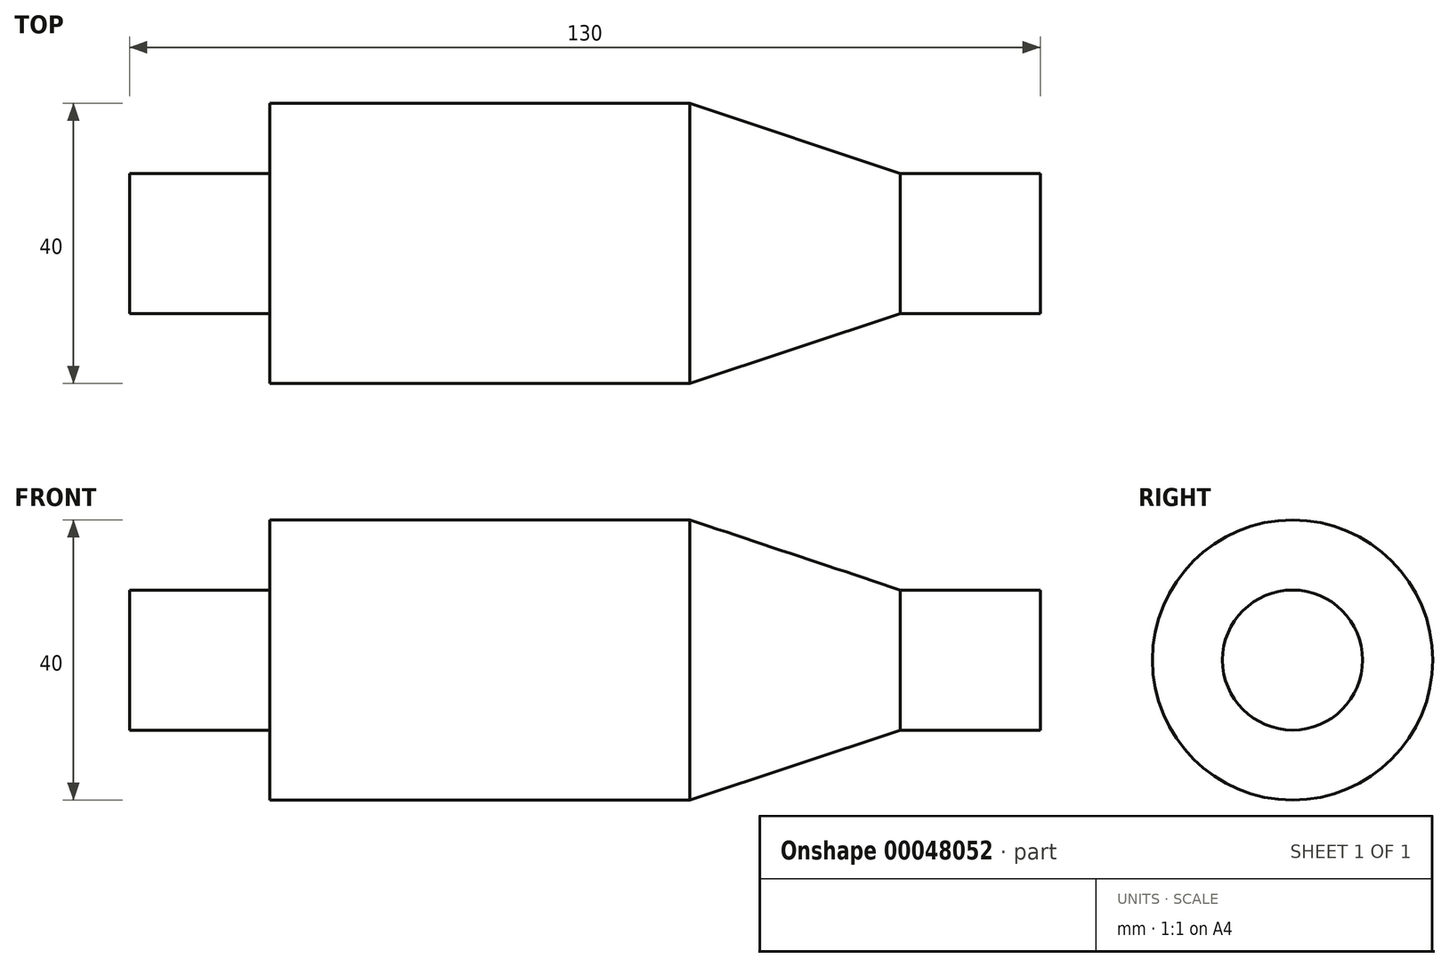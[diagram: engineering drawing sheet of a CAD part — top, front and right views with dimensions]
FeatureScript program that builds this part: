
annotation { "Feature Type Name" : "Feature", "Feature Type Description" : "" }
export const myFeature = defineFeature(function(context is Context, id is Id, definition is map)
    precondition{}
    {
        {
            var Q0;
            Q0=qCreatedBy(makeId("Front.planeOp"),FACE);
            var sketch = newSketch(context, id + "F0", { "sketchPlane" : qUnion([Q0])});
            skLineSegment(sketch, "E0", {"start": v(0, 0) * mm, "end": v(130, 0) * mm});
            skLineSegment(sketch, "E1", {"start": v(130, 0) * mm, "end": v(130, 10) * mm});
            skLineSegment(sketch, "E2", {"start": v(130, 10) * mm, "end": v(110, 10) * mm});
            skLineSegment(sketch, "E3", {"start": v(110, 10) * mm, "end": v(80, 20) * mm});
            skLineSegment(sketch, "E4", {"start": v(80, 20) * mm, "end": v(20, 20) * mm});
            skLineSegment(sketch, "E5", {"start": v(20, 20) * mm, "end": v(20, 10) * mm});
            skLineSegment(sketch, "E6", {"start": v(20, 10) * mm, "end": v(0, 10) * mm});
            skLineSegment(sketch, "E7", {"start": v(0, 10) * mm, "end": v(0, 0) * mm});
            skSolve(sketch);
        }
        {
            var Q0;
            Q0=makeQuery(id+"F0.imprint","IMPRINT",FACE,{"disambiguationData":[TD([[makeQuery(id+"F0.imprint","IMPRINT",EDGE,{"derivedFrom":sQuery(id+"F0.wireOp",EDGE,"E0")}),1.0]])]});
            var Q1;
            Q1=sQuery(id+"F0.wireOp",EDGE,"E0");
            revolve(context, id + "F1", {"entities" : qUnion([Q0]), "axis" : qUnion([Q1]), "revolveType" : RevolveType.FULL});
        }
    });
